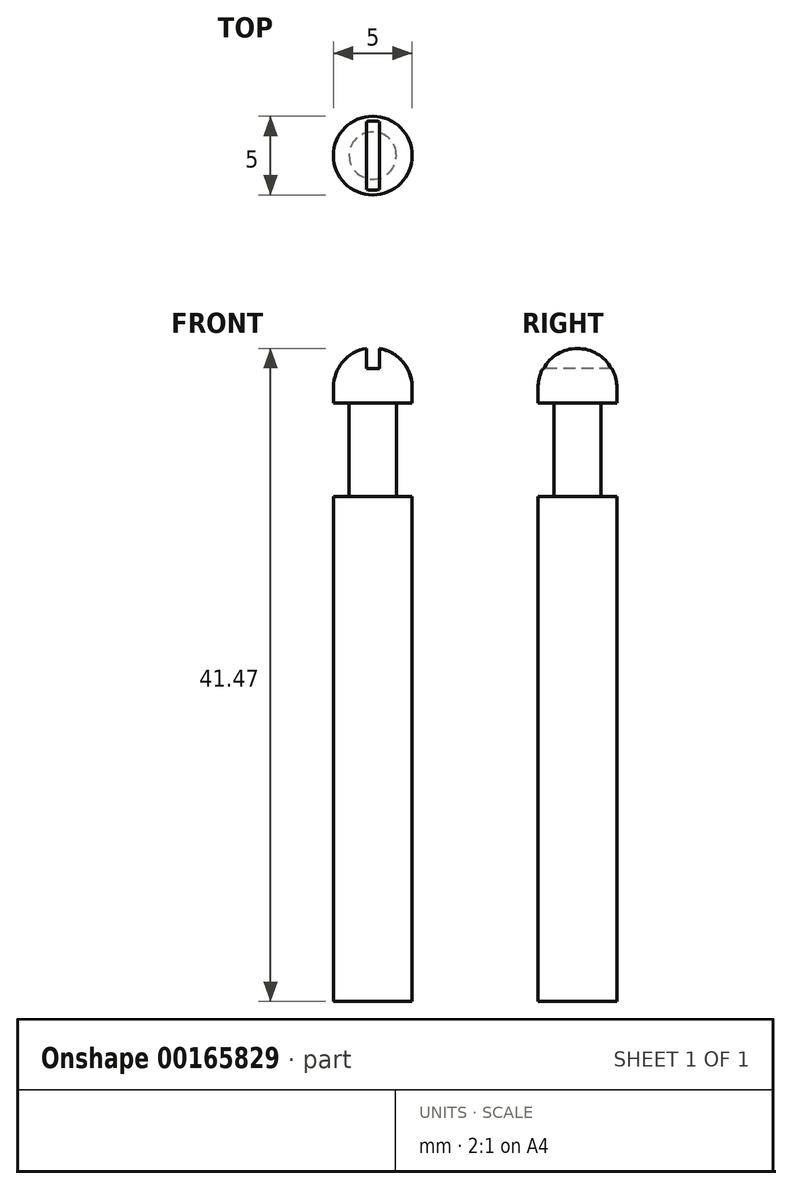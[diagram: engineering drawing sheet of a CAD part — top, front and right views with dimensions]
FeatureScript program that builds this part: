
annotation { "Feature Type Name" : "Feature", "Feature Type Description" : "" }
export const myFeature = defineFeature(function(context is Context, id is Id, definition is map)
    precondition{}
    {
        {
            var Q0;
            Q0=qCreatedBy(makeId("Front.planeOp"),FACE);
            var sketch = newSketch(context, id + "F0", { "sketchPlane" : qUnion([Q0])});
            skLineSegment(sketch, "E0.top", {"start": v(-1.5, -1) * mm, "end": v(-2.5, -1) * mm});
            skLineSegment(sketch, "E0.right", {"start": v(-2.5, 0) * mm, "end": v(-2.5, -1) * mm});
            skArc(sketch, "E1", {"start": v(-2.5, 0) * mm, "mid": v(-1.77, 1.77) * mm, "end": v(0, 2.5) * mm});
            skLineSegment(sketch, "E2.bottom", {"start": v(-1.5, -6.93) * mm, "end": v(-2.5, -6.93) * mm});
            skLineSegment(sketch, "E2.top", {"start": v(0, -39) * mm, "end": v(-2.5, -39) * mm});
            skLineSegment(sketch, "E2.right", {"start": v(-2.5, -6.93) * mm, "end": v(-2.5, -39) * mm});
            skLineSegment(sketch, "E3", {"start": v(-1.5, -1) * mm, "end": v(-1.5, -6.93) * mm});
            skLineSegment(sketch, "E4", {"start": v(0, 2.5) * mm, "end": v(0, -39) * mm, "construction": true});
            skLineSegment(sketch, "E5", {"start": v(0, 2.5) * mm, "end": v(0, -39) * mm});
            skSolve(sketch);
        }
        {
            var Q0;
            Q0=qSketchRegion(id+"F0",true);
            var Q1;
            Q1=sQuery(id+"F0.wireOp",EDGE,"E5");
            revolve(context, id + "F1", {"entities" : qUnion([Q0]), "axis" : qUnion([Q1]), "revolveType" : RevolveType.FULL});
        }
        {
            var Q0;
            Q0=qCreatedBy(makeId("Front.planeOp"),FACE);
            var sketch = newSketch(context, id + "F2", { "sketchPlane" : qUnion([Q0])});
            skLineSegment(sketch, "E6.bottom", {"start": v(-0.41, 3.5) * mm, "end": v(0, 3.5) * mm});
            skLineSegment(sketch, "E6.top", {"start": v(-0.41, 1.19) * mm, "end": v(0, 1.19) * mm});
            skLineSegment(sketch, "E6.left", {"start": v(-0.41, 3.5) * mm, "end": v(-0.41, 1.19) * mm});
            skLineSegment(sketch, "E6.right", {"start": v(0, 3.5) * mm, "end": v(0, 1.19) * mm});
            skLineSegment(sketch, "E7.MirrorCS", {"start": v(0.41, 3.5) * mm, "end": v(0.41, 1.19) * mm});
            skLineSegment(sketch, "E8.MirrorCS", {"start": v(0.41, 3.5) * mm, "end": v(0, 3.5) * mm});
            skLineSegment(sketch, "E9", {"start": v(0.41, 1.19) * mm, "end": v(0, 1.19) * mm});
            skSolve(sketch);
        }
        {
            var Q0;
            Q0=qSketchRegion(id+"F2",true);
            extrude(context, id + "F3", {"entities" : qUnion([Q0]), "operationType" : NewBodyOperationType.REMOVE, "endBound" : BoundingType.SYMMETRIC, "oppositeDirection" : true, "depth" : 25 * mm});
        }
    });
